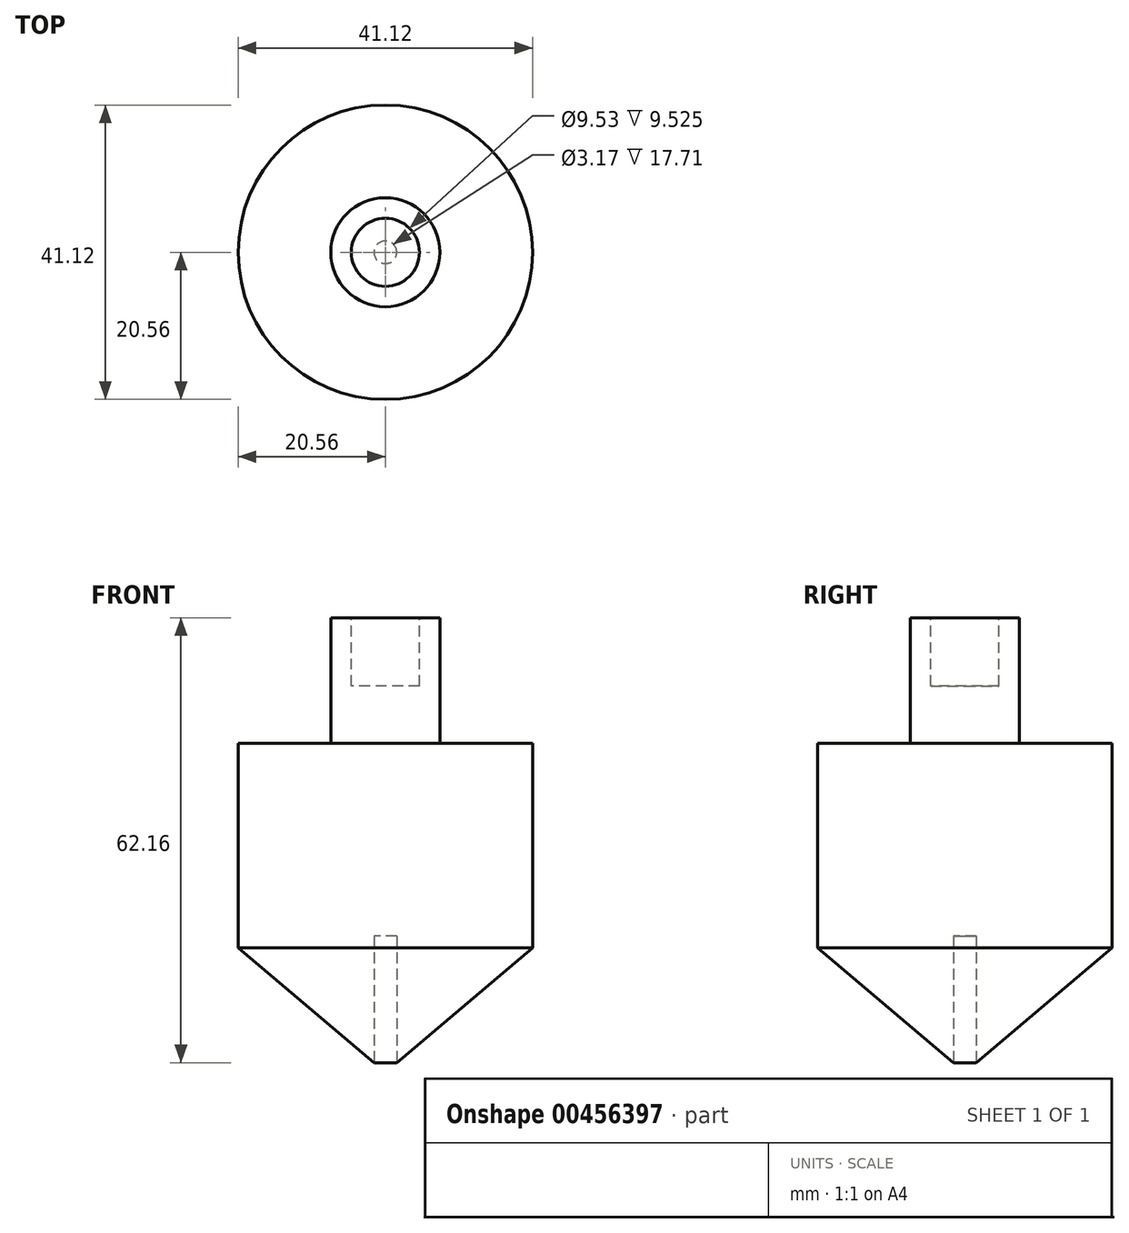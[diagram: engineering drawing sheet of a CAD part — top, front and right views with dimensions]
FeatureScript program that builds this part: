
annotation { "Feature Type Name" : "Feature", "Feature Type Description" : "" }
export const myFeature = defineFeature(function(context is Context, id is Id, definition is map)
    precondition{}
    {
        {
            var Q0;
            Q0=qCreatedBy(makeId("Front.planeOp"),FACE);
            var sketch = newSketch(context, id + "F0", { "sketchPlane" : qUnion([Q0])});
            skLineSegment(sketch, "E0", {"start": v(0, 0) * mm, "end": v(20.56, 17.35) * mm});
            skLineSegment(sketch, "E1", {"start": v(20.56, 17.35) * mm, "end": v(20.56, 55.45) * mm});
            skLineSegment(sketch, "E2", {"start": v(20.56, 55.45) * mm, "end": v(7.62, 55.45) * mm});
            skLineSegment(sketch, "E3", {"start": v(7.62, 55.45) * mm, "end": v(7.62, 63.5) * mm});
            skLineSegment(sketch, "E4", {"start": v(7.62, 63.5) * mm, "end": v(0, 63.5) * mm});
            skLineSegment(sketch, "E5", {"start": v(0, 63.5) * mm, "end": v(0, 0) * mm});
            skSolve(sketch);
        }
        {
            var Q0;
            Q0=makeQuery(id+"F0.imprint","IMPRINT",FACE,{"disambiguationData":[TD([[makeQuery(id+"F0.imprint","IMPRINT",EDGE,{"derivedFrom":sQuery(id+"F0.wireOp",EDGE,"E0")}),1.0]])]});
            var Q1;
            Q1=sQuery(id+"F0.wireOp",EDGE,"E5");
            revolve(context, id + "F1", {"entities" : qUnion([Q0]), "axis" : qUnion([Q1]), "revolveType" : RevolveType.FULL});
        }
        {
            var Q0;
            Q0=makeQuery(id+"F1.opRevolve","SWEPT_FACE",FACE,{"disambiguationData":[OSD([sQuery(id+"F0.wireOp",EDGE,"E4")])]});
            var sketch = newSketch(context, id + "F2", { "sketchPlane" : qUnion([Q0])});
            skCircle(sketch, "E6", {"center": v(0, 0) * mm, "radius": 4.76 * mm});
            skSolve(sketch);
        }
        {
            var Q0;
            Q0 = qSketchRegion(id + "F2", true);
            var Q1;
            Q1=makeQuery(id+"F1.opRevolve","SWEPT_FACE",FACE,{"disambiguationData":[OSD([sQuery(id+"F0.wireOp",EDGE,"E2")])]});
            extrude(context, id + "F3", {"entities" : qUnion([Q0, Q1]), "operationType" : NewBodyOperationType.REMOVE, "oppositeDirection" : true, "depth" : 9.52 * mm});
        }
        {
            var Q0;
            Q0=qCreatedBy(makeId("Top.planeOp"),FACE);
            var sketch = newSketch(context, id + "F4", { "sketchPlane" : qUnion([Q0])});
            skCircle(sketch, "E7", {"center": v(0, 0) * mm, "radius": 1.59 * mm});
            skSolve(sketch);
        }
        {
            var Q0;
            Q0 = qSketchRegion(id + "F4", true);
            extrude(context, id + "F5", {"entities" : qUnion([Q0]), "operationType" : NewBodyOperationType.REMOVE, "depth" : 19.05 * mm});
        }
    });
